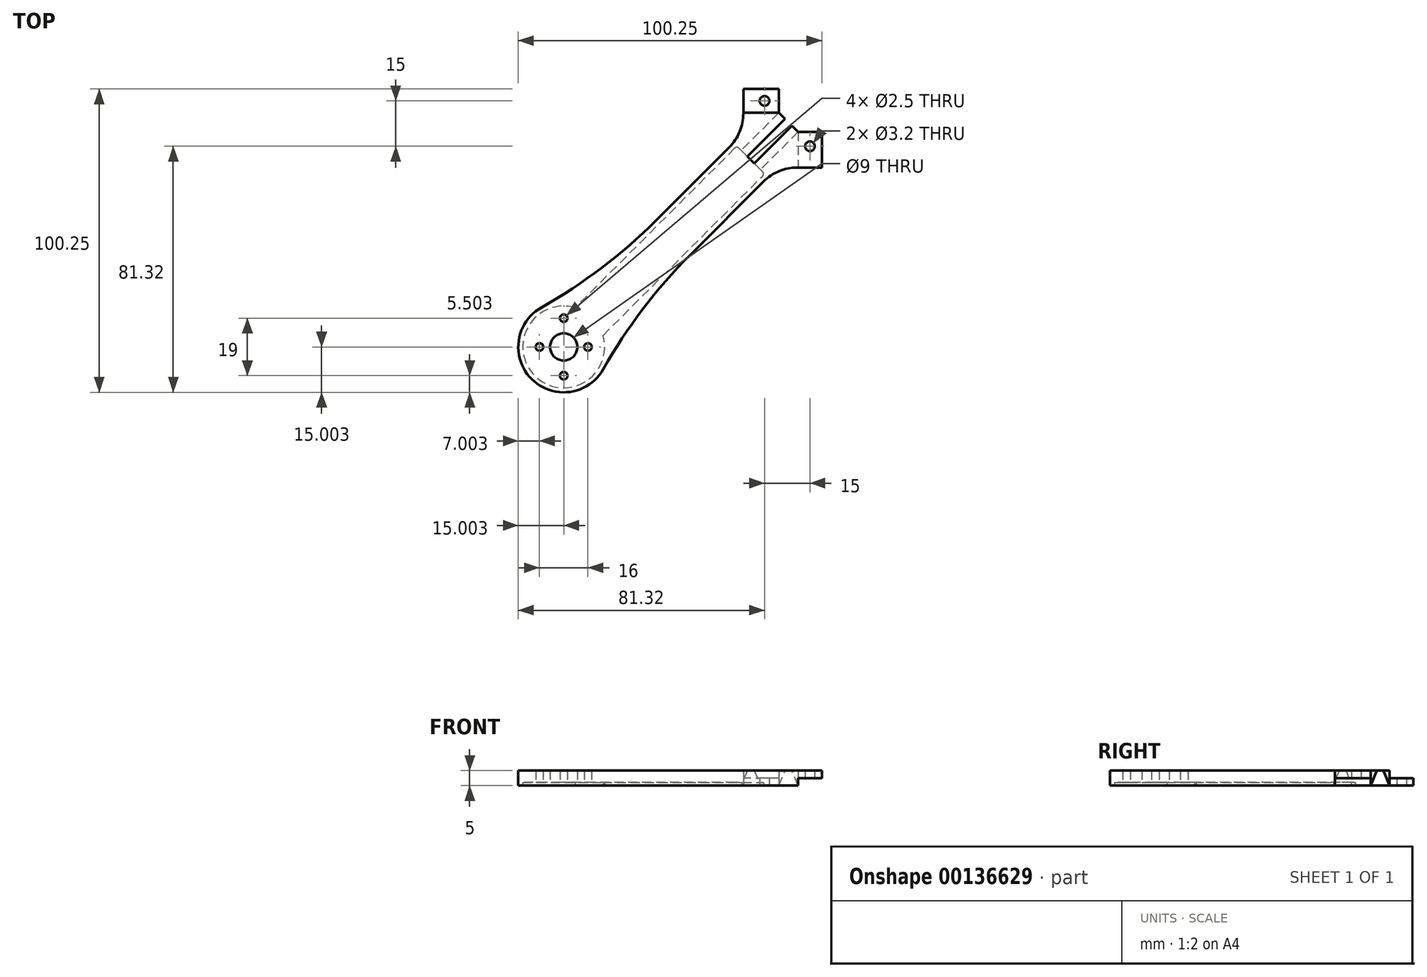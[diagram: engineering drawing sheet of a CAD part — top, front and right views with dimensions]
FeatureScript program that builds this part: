
annotation { "Feature Type Name" : "Feature", "Feature Type Description" : "" }
export const myFeature = defineFeature(function(context is Context, id is Id, definition is map)
    precondition{}
    {
        {
            var Q0;
            Q0=qCreatedBy(makeId("Top.planeOp"),FACE);
            var sketch = newSketch(context, id + "F0", { "sketchPlane" : qUnion([Q0])});
            skLineSegment(sketch, "E0.left", {"start": v(-22, 3.93) * mm, "end": v(-22, -4.06) * mm});
            skLineSegment(sketch, "E1.top", {"start": v(-18, -18) * mm, "end": v(3.93, -18) * mm, "construction": true});
            skLineSegment(sketch, "E1.left", {"start": v(-18, 3.93) * mm, "end": v(-18, -18) * mm, "construction": true});
            skCircle(sketch, "E2.MirrorC", {"center": v(-15, -15) * mm, "radius": 1.6 * mm, "construction": true});
            skCircle(sketch, "E3.MirrorC", {"center": v(-89.32, -81.32) * mm, "radius": 1.25 * mm});
            skCircle(sketch, "E4.MirrorC", {"center": v(-81.32, -71.82) * mm, "radius": 1.25 * mm});
            skCircle(sketch, "E5.MirrorC", {"center": v(-81.32, -90.82) * mm, "radius": 1.25 * mm});
            skCircle(sketch, "E6.MirrorC", {"center": v(-73.32, -81.32) * mm, "radius": 1.25 * mm});
            skCircle(sketch, "E7.MirrorC", {"center": v(-81.32, -81.32) * mm, "radius": 4.5 * mm});
            skCircle(sketch, "E8.MirrorC", {"center": v(-81.32, -81.32) * mm, "radius": 13.85 * mm, "construction": true});
            skArc(sketch, "E9.MirrorC", {"start": v(-66.69, -78) * mm, "mid": v(-91.92, -91.92) * mm, "end": v(-78, -66.69) * mm});
            skPoint(sketch, "E10", {"position": v(-22, 0) * mm});
            skPoint(sketch, "E11", {"position": v(0, -22) * mm});
            skLineSegment(sketch, "E12", {"start": v(-22, 0) * mm, "end": v(0, 0) * mm, "construction": true});
            skLineSegment(sketch, "E13", {"start": v(0, -22) * mm, "end": v(0, 0) * mm, "construction": true});
            skLineSegment(sketch, "E14.1", {"start": v(0.6, -5.56) * mm, "end": v(-0.6, -5.56) * mm, "construction": true});
            skLineSegment(sketch, "E15.trimOffspring", {"start": v(-3.93, -10.27) * mm, "end": v(-3.93, -22) * mm});
            skLineSegment(sketch, "E16.trimOffspring", {"start": v(-10.27, -3.93) * mm, "end": v(-22, -3.93) * mm});
            skCircle(sketch, "E17", {"center": v(-15, 0) * mm, "radius": 1.6 * mm});
            skCircle(sketch, "E18", {"center": v(0, -15) * mm, "radius": 1.6 * mm});
            skLineSegment(sketch, "E19", {"start": v(0, 0) * mm, "end": v(-70.71, -70.71) * mm, "construction": true});
            skLineSegment(sketch, "E20", {"start": v(-3.93, -8.88) * mm, "end": v(-0.6, -5.56) * mm, "construction": true});
            skLineSegment(sketch, "E21.trimOffspring", {"start": v(-5.56, -0.6) * mm, "end": v(-8.88, -3.93) * mm, "construction": true});
            skLineSegment(sketch, "E22", {"start": v(-26.69, -15.37) * mm, "end": v(-78, -66.69) * mm});
            skLineSegment(sketch, "E23", {"start": v(-66.69, -78) * mm, "end": v(-15.37, -26.69) * mm});
            skLineSegment(sketch, "E24", {"start": v(-23.41, -15.64) * mm, "end": v(-15.64, -23.41) * mm});
            skLineSegment(sketch, "E25.0", {"start": v(-68.35, -77.55) * mm, "end": v(-15.64, -24.83) * mm});
            skArc(sketch, "E25.1", {"start": v(-68.35, -77.55) * mm, "mid": v(-90.86, -90.86) * mm, "end": v(-77.55, -68.35) * mm});
            skLineSegment(sketch, "E25.2", {"start": v(-24.83, -15.64) * mm, "end": v(-77.55, -68.35) * mm});
            skLineSegment(sketch, "E26.trimOffspring", {"start": v(-4.06, -22) * mm, "end": v(3.93, -22) * mm});
            skPoint(sketch, "E27.visualSharp", {"position": v(-24.12, -14.93) * mm});
            skArc(sketch, "E27.filletArc", {"start": v(-23.41, -15.64) * mm, "mid": v(-24.12, -15.34) * mm, "end": v(-24.83, -15.64) * mm});
            skPoint(sketch, "E28.visualSharp", {"position": v(-14.93, -24.12) * mm});
            skArc(sketch, "E28.filletArc", {"start": v(-15.64, -24.83) * mm, "mid": v(-15.34, -24.12) * mm, "end": v(-15.64, -23.41) * mm});
            skPoint(sketch, "E29.visualSharp", {"position": v(-10.69, -22) * mm});
            skArc(sketch, "E29.filletArc", {"start": v(-4.06, -22) * mm, "mid": v(-10.18, -23.22) * mm, "end": v(-15.37, -26.69) * mm});
            skPoint(sketch, "E30.visualSharp", {"position": v(-22, -10.69) * mm});
            skArc(sketch, "E30.filletArc", {"start": v(-26.69, -15.37) * mm, "mid": v(-23.22, -10.18) * mm, "end": v(-22, -4.06) * mm});
            skLineSegment(sketch, "E31", {"start": v(-8.88, -3.93) * mm, "end": v(-3.93, -8.88) * mm, "construction": true});
            skLineSegment(sketch, "E32", {"start": v(-8.23, -5.97) * mm, "end": v(-20.66, -18.4) * mm});
            skLineSegment(sketch, "E33", {"start": v(-5.97, -8.23) * mm, "end": v(-18.4, -20.66) * mm});
            skLineSegment(sketch, "E34", {"start": v(0.6, -5.56) * mm, "end": v(3.93, -8.88) * mm, "construction": true});
            skLineSegment(sketch, "E35", {"start": v(-5.56, 0.6) * mm, "end": v(-8.88, 3.93) * mm, "construction": true});
            skLineSegment(sketch, "E36", {"start": v(-5.56, 0.6) * mm, "end": v(-5.56, -0.6) * mm, "construction": true});
            skLineSegment(sketch, "E37", {"start": v(-3.93, -8.88) * mm, "end": v(3.93, -8.88) * mm, "construction": true});
            skLineSegment(sketch, "E38", {"start": v(3.93, -22) * mm, "end": v(3.93, -10.27) * mm});
            skLineSegment(sketch, "E39", {"start": v(-8.88, -3.93) * mm, "end": v(-8.88, 3.93) * mm, "construction": true});
            skLineSegment(sketch, "E40", {"start": v(-22, 3.93) * mm, "end": v(-10.27, 3.93) * mm});
            skLineSegment(sketch, "E41", {"start": v(-8.88, 3.93) * mm, "end": v(-8.44, 3.93) * mm, "construction": true});
            skLineSegment(sketch, "E42", {"start": v(-8.44, 3.93) * mm, "end": v(-8.44, 2.53) * mm, "construction": true});
            skLineSegment(sketch, "E43", {"start": v(-8.44, 2.53) * mm, "end": v(-8.88, 2.53) * mm, "construction": true});
            skLineSegment(sketch, "E44", {"start": v(-8.88, 3.93) * mm, "end": v(-8.88, 4.28) * mm, "construction": true});
            skLineSegment(sketch, "E45", {"start": v(-8.88, 4.28) * mm, "end": v(-10.27, 4.28) * mm, "construction": true});
            skLineSegment(sketch, "E46", {"start": v(-10.27, 4.28) * mm, "end": v(-10.27, 3.93) * mm, "construction": true});
            skLineSegment(sketch, "E47", {"start": v(-8.88, 2.53) * mm, "end": v(-10.27, 3.93) * mm, "construction": true});
            skLineSegment(sketch, "E48", {"start": v(-10.27, 3.93) * mm, "end": v(-10.27, -3.93) * mm});
            skLineSegment(sketch, "E49", {"start": v(-10.27, -3.93) * mm, "end": v(-3.93, -10.27) * mm});
            skLineSegment(sketch, "E50", {"start": v(-3.93, -10.27) * mm, "end": v(3.93, -10.27) * mm});
            skLineSegment(sketch, "E51.trimOffspring", {"start": v(-8.88, 3.93) * mm, "end": v(-8.88, 3.93) * mm});
            skLineSegment(sketch, "E52.trimOffspring", {"start": v(3.93, -8.88) * mm, "end": v(3.93, -8.88) * mm});
            skLineSegment(sketch, "E53", {"start": v(-10.27, 3.93) * mm, "end": v(-8.88, 3.93) * mm, "construction": true});
            skLineSegment(sketch, "E54", {"start": v(-10.27, -3.93) * mm, "end": v(-8.88, -3.93) * mm, "construction": true});
            skLineSegment(sketch, "E55", {"start": v(-3.93, -8.88) * mm, "end": v(-3.93, -10.27) * mm, "construction": true});
            skLineSegment(sketch, "E56", {"start": v(3.93, -8.88) * mm, "end": v(3.93, -10.27) * mm, "construction": true});
            skPoint(sketch, "E57.orphan", {"position": v(-7.54, -5.27) * mm});
            skLineSegment(sketch, "E58", {"start": v(-8.23, -5.97) * mm, "end": v(-7.54, -5.27) * mm, "construction": true});
            skLineSegment(sketch, "E59", {"start": v(-5.97, -8.23) * mm, "end": v(-5.27, -7.54) * mm, "construction": true});
            skSolve(sketch);
        }
        {
            var Q0;
            {var subQ0=sQuery(id+"F0.wireOp",EDGE,"E16.trimOffspring");var subQ1=sQuery(id+"F0.wireOp",EDGE,"E0.left");var subQ2=makeQuery(id+"F0.imprint","INTERSECT",VERTEX,{"derivedFrom":[subQ1,subQ0]});Q0=makeQuery(id+"F0.imprint","IMPRINT",FACE,{"disambiguationData":[TD([[makeQuery(id+"F0.imprint","IMPRINT",EDGE,{"disambiguationData":[TD([[subQ2,-1.0]])],"derivedFrom":subQ1}),1.0]])]});}
            var Q1;
            Q1=makeQuery(id+"F0.imprint","IMPRINT",FACE,{"disambiguationData":[TD([[makeQuery(id+"F0.imprint","IMPRINT",EDGE,{"derivedFrom":sQuery(id+"F0.wireOp",EDGE,"E9.MirrorC")}),-1.0]])]});
            var Q2;
            {var subQ1=sQuery(id+"F0.wireOp",EDGE,"E0.top");var subQ5=makeQuery(id+"F0.imprint","INTERSECT",VERTEX,{"derivedFrom":[subQ1,sQuery(id+"F0.wireOp",EDGE,"E23")]});Q2=makeQuery(id+"F0.imprint","IMPRINT",FACE,{"disambiguationData":[TD([[makeQuery(id+"F0.imprint","IMPRINT",EDGE,{"disambiguationData":[TD([[subQ5,1.0]])],"derivedFrom":subQ1}),1.0]])]});}
            var Q3;
            Q3=makeQuery(id+"F0.imprint","IMPRINT",FACE,{"disambiguationData":[TD([[makeQuery(id+"F0.imprint","IMPRINT",EDGE,{"derivedFrom":sQuery(id+"F0.wireOp",EDGE,"E3.MirrorC")}),-1.0]])]});
            extrude(context, id + "F1", {"entities" : qUnion([Q0, Q1, Q2, Q3]), "depth" : 5 * mm});
        }
        {
            var Q0;
            {var subQ0=sQuery(id+"F0.wireOp",EDGE,"E16.trimOffspring");Q0=makeQuery(id+"F0.imprint","IMPRINT",FACE,{"disambiguationData":[TD([[makeQuery(id+"F0.imprint","IMPRINT",EDGE,{"derivedFrom":subQ0}),-1.0]])]});}
            extrude(context, id + "F2", {"entities" : qUnion([Q0]), "operationType" : NewBodyOperationType.ADD, "depth" : 2.5 * mm});
        }
        {
            var Q0;
            {var subQ2=sQuery(id+"F0.wireOp",EDGE,"E15.trimOffspring");Q0=makeQuery(id+"F0.imprint","IMPRINT",FACE,{"disambiguationData":[TD([[makeQuery(id+"F0.imprint","IMPRINT",EDGE,{"derivedFrom":subQ2}),1.0]])]});}
            extrude(context, id + "F3", {"entities" : qUnion([Q0]), "operationType" : NewBodyOperationType.ADD, "depth" : 5 * mm});
        }
        {
            var Q0;
            {var subQ2=sQuery(id+"F0.wireOp",EDGE,"E15.trimOffspring");Q0=makeQuery(id+"F0.imprint","IMPRINT",FACE,{"disambiguationData":[TD([[makeQuery(id+"F0.imprint","IMPRINT",EDGE,{"derivedFrom":subQ2}),1.0]])]});}
            extrude(context, id + "F4", {"entities" : qUnion([Q0]), "operationType" : NewBodyOperationType.REMOVE, "depth" : 2.5 * mm});
        }
        {
            var Q0;
            Q0=makeQuery(id+"F0.imprint","IMPRINT",FACE,{"disambiguationData":[TD([[makeQuery(id+"F0.imprint","IMPRINT",EDGE,{"derivedFrom":sQuery(id+"F0.wireOp",EDGE,"E3.MirrorC")}),-1.0]])]});
            var Q1;
            {var subQ3=sQuery(id+"F0.wireOp",EDGE,"E24");Q1=makeQuery(id+"F0.imprint","IMPRINT",FACE,{"disambiguationData":[TD([[makeQuery(id+"F0.imprint","IMPRINT",EDGE,{"derivedFrom":subQ3}),-1.0]])]});}
            extrude(context, id + "F5", {"entities" : qUnion([Q0, Q1]), "operationType" : NewBodyOperationType.REMOVE, "depth" : 1 * mm});
        }
        {
            var Q0;
            Q0=makeQuery(id+"F1.opExtrude","SWEPT_EDGE",EDGE,{"disambiguationData":[OSD([sQuery(id+"F0.wireOp",EDGE,"E9.MirrorC"),sQuery(id+"F0.wireOp",EDGE,"E23")])]});
            var Q1;
            Q1=makeQuery(id+"F1.opExtrude","SWEPT_EDGE",EDGE,{"disambiguationData":[OSD([sQuery(id+"F0.wireOp",EDGE,"E9.MirrorC"),sQuery(id+"F0.wireOp",EDGE,"E22")])]});
            fillet(context, id + "F6", {"entities" : qUnion([Q0, Q1]), "radius" : 175 * mm, "tangentPropagation" : true, "allowEdgeOverflow" : false});
        }
        {
            var Q0;
            Q0=makeQuery(id+"F1.opExtrude","SWEPT_FACE",FACE,{"disambiguationData":[OSD([sQuery(id+"F0.wireOp",EDGE,"E24")])]});
            var sketch = newSketch(context, id + "F7", { "sketchPlane" : qUnion([Q0])});
            skLineSegment(sketch, "E60", {"start": v(1.6, 5) * mm, "end": v(4.49, 0) * mm});
            skLineSegment(sketch, "E61", {"start": v(-1.6, 5) * mm, "end": v(-4.49, 0) * mm});
            skLineSegment(sketch, "E62", {"start": v(-4.49, 0) * mm, "end": v(4.49, 0) * mm});
            skLineSegment(sketch, "E63", {"start": v(-1.6, 5) * mm, "end": v(1.6, 5) * mm});
            skSolve(sketch);
        }
        {
            var Q0;
            Q0=makeQuery(id+"F7.imprint","IMPRINT",FACE,{"disambiguationData":[TD([[makeQuery(id+"F7.imprint","IMPRINT",EDGE,{"derivedFrom":sQuery(id+"F7.wireOp",EDGE,"E60")}),-1.0]])]});
            extrude(context, id + "F8", {"entities" : qUnion([Q0]), "operationType" : NewBodyOperationType.REMOVE, "depth" : 25 * mm});
        }
    });
